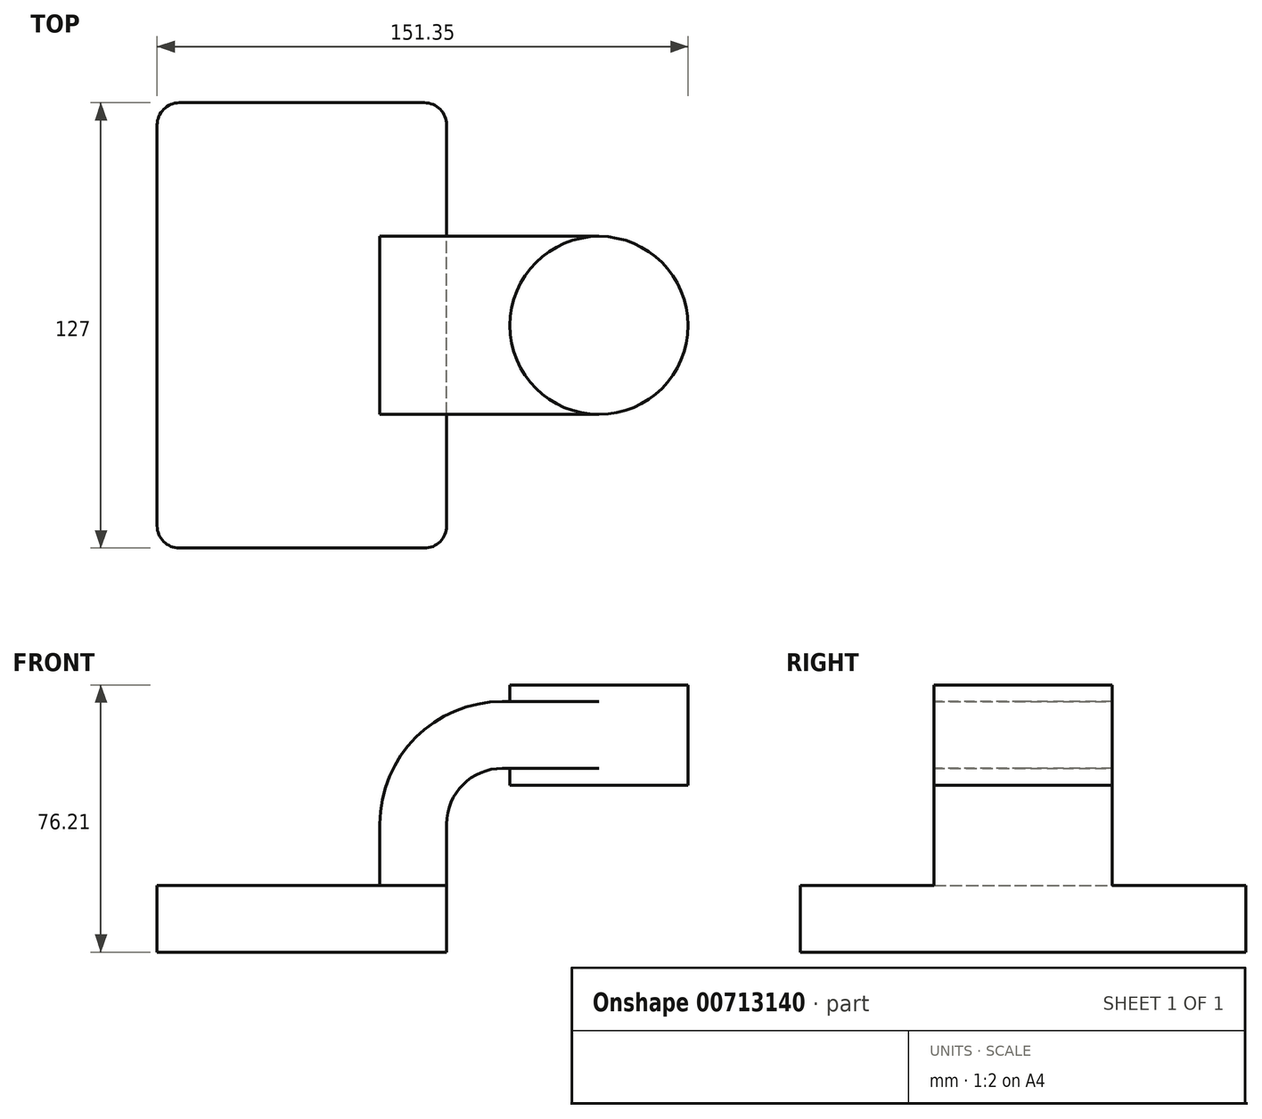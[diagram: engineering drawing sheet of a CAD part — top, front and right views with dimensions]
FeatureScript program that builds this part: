
annotation { "Feature Type Name" : "Feature", "Feature Type Description" : "" }
export const myFeature = defineFeature(function(context is Context, id is Id, definition is map)
    precondition{}
    {
        {
            var Q0;
            Q0=qCreatedBy(makeId("Front.planeOp"),FACE);
            var sketch = newSketch(context, id + "F0", { "sketchPlane" : qUnion([Q0])});
            skLineSegment(sketch, "E0.bottom", {"start": v(41.28, -9.52) * mm, "end": v(-41.28, -9.53) * mm});
            skLineSegment(sketch, "E0.top", {"start": v(41.28, 9.53) * mm, "end": v(-41.28, 9.53) * mm});
            skLineSegment(sketch, "E0.left", {"start": v(41.28, -9.52) * mm, "end": v(41.28, 9.53) * mm});
            skLineSegment(sketch, "E0.right", {"start": v(-41.28, -9.53) * mm, "end": v(-41.28, 9.53) * mm});
            skPoint(sketch, "E0.middle", {"position": v(0, 0) * mm});
            skLineSegment(sketch, "E1.bottom", {"start": v(110.08, 66.68) * mm, "end": v(59.28, 66.68) * mm});
            skLineSegment(sketch, "E1.top", {"start": v(110.08, 38.1) * mm, "end": v(59.28, 38.1) * mm});
            skLineSegment(sketch, "E1.left", {"start": v(110.08, 66.68) * mm, "end": v(110.08, 38.1) * mm});
            skLineSegment(sketch, "E1.right", {"start": v(59.28, 66.68) * mm, "end": v(59.28, 38.1) * mm});
            skPoint(sketch, "E1.middle", {"position": v(84.68, 52.39) * mm});
            skLineSegment(sketch, "E2", {"start": v(41.28, 9.53) * mm, "end": v(41.28, 27) * mm});
            skArc(sketch, "E3", {"start": v(41.27, 27) * mm, "mid": v(45.92, 38.23) * mm, "end": v(57.15, 42.88) * mm});
            skLineSegment(sketch, "E4", {"start": v(57.15, 42.88) * mm, "end": v(84.68, 42.88) * mm});
            skLineSegment(sketch, "E5.0", {"start": v(57.15, 61.93) * mm, "end": v(84.68, 61.93) * mm});
            skArc(sketch, "E5.1", {"start": v(22.23, 27) * mm, "mid": v(32.45, 51.7) * mm, "end": v(57.15, 61.93) * mm});
            skLineSegment(sketch, "E5.2", {"start": v(22.22, 9.53) * mm, "end": v(22.22, 27) * mm});
            skLineSegment(sketch, "E6", {"start": v(84.68, 38.1) * mm, "end": v(84.68, 66.68) * mm});
            skFitSpline(sketch, "E7", {"points": [v(-41.28, 9.53) * mm, v(57.15, 61.93) * mm], "startDerivative": vector(10.36, 68.73) * mm, "endDerivative": vector(216.6, -3.8) * mm});
            skSolve(sketch);
        }
        {
            var Q0;
            Q0=makeQuery(id+"F0.imprint","IMPRINT",FACE,{"disambiguationData":[TD([[makeQuery(id+"F0.imprint","IMPRINT",EDGE,{"derivedFrom":sQuery(id+"F0.wireOp",EDGE,"E0.bottom")}),-1.0]])]});
            extrude(context, id + "F1", {"entities" : qUnion([Q0]), "endBound" : BoundingType.SYMMETRIC, "depth" : 127 * mm, "offsetDistance" : 25.4 * mm});
        }
        {
            var Q0;
            {var subQ1=sQuery(id+"F0.wireOp",EDGE,"E2");Q0=makeQuery(id+"F0.imprint","IMPRINT",FACE,{"disambiguationData":[TD([[makeQuery(id+"F0.imprint","IMPRINT",EDGE,{"derivedFrom":subQ1}),1.0]])]});}
            var Q1;
            {var subQ0=sQuery(id+"F0.wireOp",EDGE,"E5.0");var subQ1=sQuery(id+"F0.wireOp",EDGE,"E1.right");var subQ2=makeQuery(id+"F0.imprint","INTERSECT",VERTEX,{"derivedFrom":[subQ1,subQ0]});Q1=makeQuery(id+"F0.imprint","IMPRINT",FACE,{"disambiguationData":[TD([[makeQuery(id+"F0.imprint","IMPRINT",EDGE,{"disambiguationData":[TD([[subQ2,-1.0]])],"derivedFrom":subQ1}),1.0]])]});}
            extrude(context, id + "F2", {"entities" : qUnion([Q0, Q1]), "operationType" : NewBodyOperationType.ADD, "endBound" : BoundingType.SYMMETRIC, "depth" : 50.8 * mm, "offsetDistance" : 25.4 * mm});
        }
        {
            var Q0;
            Q0=makeQuery(id+"F0.imprint","IMPRINT",FACE,{"disambiguationData":[TD([[makeQuery(id+"F0.imprint","IMPRINT",EDGE,{"derivedFrom":sQuery(id+"F0.wireOp",EDGE,"E5.1")}),1.0]])]});
            extrude(context, id + "F3", {"entities" : qUnion([Q0]), "operationType" : NewBodyOperationType.ADD, "endBound" : BoundingType.SYMMETRIC, "depth" : 15.88 * mm, "offsetDistance" : 25.4 * mm});
        }
        {
            var Q0;
            {var subQ4=sQuery(id+"F0.wireOp",EDGE,"E1.left");Q0=makeQuery(id+"F0.imprint","IMPRINT",FACE,{"disambiguationData":[TD([[makeQuery(id+"F0.imprint","IMPRINT",EDGE,{"derivedFrom":subQ4}),-1.0]])]});}
            var Q1;
            Q1=sQuery(id+"F0.wireOp",EDGE,"E6");
            revolve(context, id + "F4", {"operationType" : NewBodyOperationType.ADD, "surfaceOperationType" : NewSurfaceOperationType.NEW, "entities" : qUnion([Q0]), "axis" : qUnion([Q1]), "revolveType" : RevolveType.FULL});
        }
        {
            var Q0;
            Q0=makeQuery(id+"F1.opExtrude","CAP_EDGE",EDGE,{"disambiguationData":[OSD([sQuery(id+"F0.wireOp",EDGE,"E0.left")])],"isStart":false});
            var Q1;
            Q1=makeQuery(id+"F1.opExtrude","CAP_EDGE",EDGE,{"disambiguationData":[OSD([sQuery(id+"F0.wireOp",EDGE,"E0.right")])],"isStart":false});
            var Q2;
            Q2=makeQuery(id+"F1.opExtrude","CAP_EDGE",EDGE,{"disambiguationData":[OSD([sQuery(id+"F0.wireOp",EDGE,"E0.left")])],"isStart":true});
            var Q3;
            Q3=makeQuery(id+"F1.opExtrude","CAP_EDGE",EDGE,{"disambiguationData":[OSD([sQuery(id+"F0.wireOp",EDGE,"E0.right")])],"isStart":true});
            fillet(context, id + "F5", {"entities" : qUnion([Q0, Q1, Q2, Q3]), "radius" : 6.35 * mm, "tangentPropagation" : true, "allowEdgeOverflow" : false});
        }
    });
